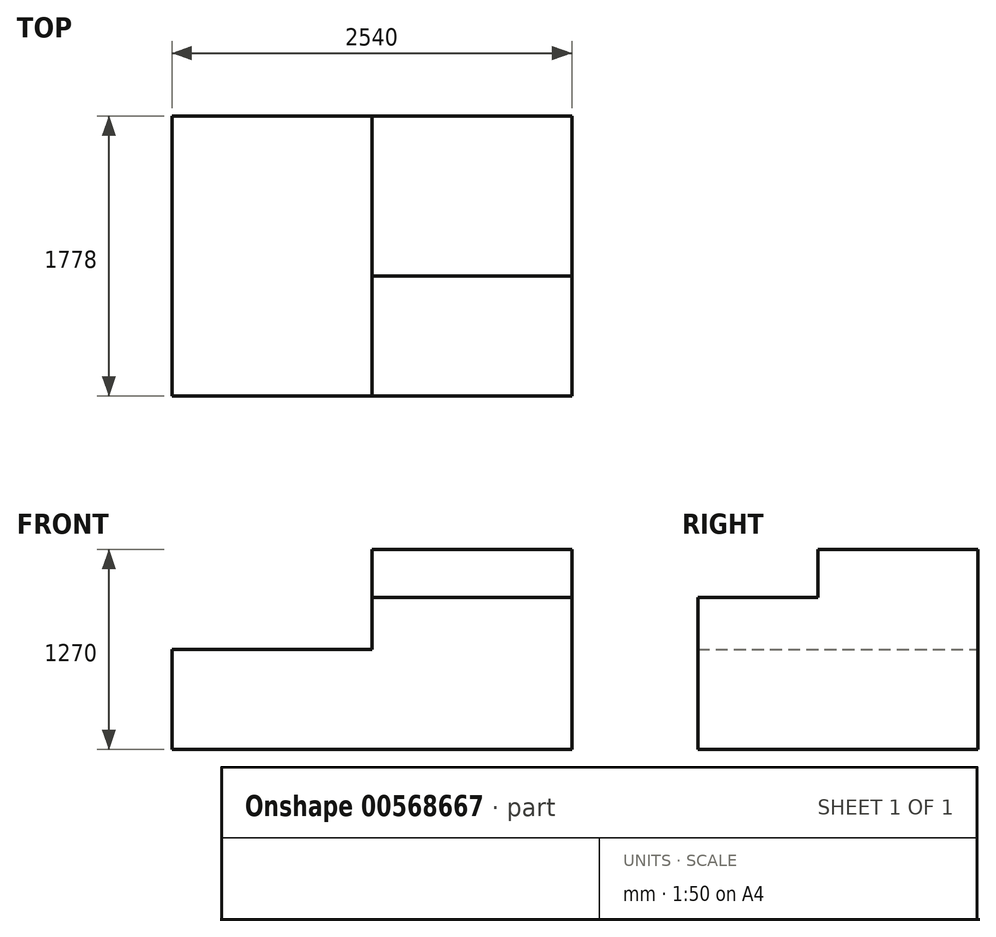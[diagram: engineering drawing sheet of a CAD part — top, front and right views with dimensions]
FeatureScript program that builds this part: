
annotation { "Feature Type Name" : "Feature", "Feature Type Description" : "" }
export const myFeature = defineFeature(function(context is Context, id is Id, definition is map)
    precondition{}
    {
        {
            var Q0;
            Q0=qCreatedBy(makeId("Top.planeOp"),FACE);
            var sketch = newSketch(context, id + "F0", { "sketchPlane" : qUnion([Q0])});
            skLineSegment(sketch, "E0.bottom", {"start": v(0, 0) * mm, "end": v(2540, 0) * mm});
            skLineSegment(sketch, "E0.top", {"start": v(0, -1778) * mm, "end": v(2540, -1778) * mm});
            skLineSegment(sketch, "E0.left", {"start": v(0, 0) * mm, "end": v(0, -1778) * mm});
            skLineSegment(sketch, "E0.right", {"start": v(2540, 0) * mm, "end": v(2540, -1778) * mm});
            skSolve(sketch);
        }
        {
            var Q0;
            Q0=makeQuery(id+"F0.imprint","IMPRINT",FACE,{"disambiguationData":[TD([[makeQuery(id+"F0.imprint","IMPRINT",EDGE,{"derivedFrom":sQuery(id+"F0.wireOp",EDGE,"E0.bottom")}),-1.0]])]});
            extrude(context, id + "F1", {"entities" : qUnion([Q0]), "depth" : 1270 * mm, "offsetDistance" : 25.4 * mm});
        }
        {
            var Q0;
            Q0=makeQuery(id+"F1.opExtrude","SWEPT_FACE",FACE,{"disambiguationData":[OSD([sQuery(id+"F0.wireOp",EDGE,"E0.left")])]});
            var sketch = newSketch(context, id + "F2", { "sketchPlane" : qUnion([Q0])});
            skLineSegment(sketch, "E1.bottom", {"start": v(1778, 0) * mm, "end": v(0, 0) * mm});
            skLineSegment(sketch, "E1.top", {"start": v(1778, 635) * mm, "end": v(0, 635) * mm});
            skLineSegment(sketch, "E1.left", {"start": v(1778, 0) * mm, "end": v(1778, 635) * mm});
            skLineSegment(sketch, "E1.right", {"start": v(0, 0) * mm, "end": v(0, 635) * mm});
            skSolve(sketch);
        }
        {
            var Q0;
            {var subQ0=sQuery(id+"F2.wireOp",EDGE,"E1.top");Q0=makeQuery(id+"F2.imprint","IMPRINT",FACE,{"disambiguationData":[TD([[makeQuery(id+"F2.imprint","IMPRINT",EDGE,{"derivedFrom":subQ0}),-1.0]])]});}
            extrude(context, id + "F3", {"entities" : qUnion([Q0]), "operationType" : NewBodyOperationType.REMOVE, "oppositeDirection" : true, "depth" : 1270 * mm, "offsetDistance" : 25.4 * mm});
        }
        {
            var Q0;
            Q0=makeQuery(id+"F1.opExtrude","CAP_FACE",FACE,{"disambiguationData":[OSD([sQuery(id+"F0.wireOp",EDGE,"E0.bottom"),sQuery(id+"F0.wireOp",EDGE,"E0.top"),sQuery(id+"F0.wireOp",EDGE,"E0.left"),sQuery(id+"F0.wireOp",EDGE,"E0.right")])],"isStart":false});
            var sketch = newSketch(context, id + "F4", { "sketchPlane" : qUnion([Q0])});
            skLineSegment(sketch, "E2.bottom", {"start": v(2540, 0) * mm, "end": v(1270, 0) * mm});
            skLineSegment(sketch, "E2.top", {"start": v(2540, -1016) * mm, "end": v(1270, -1016) * mm});
            skLineSegment(sketch, "E2.left", {"start": v(2540, 0) * mm, "end": v(2540, -1016) * mm});
            skLineSegment(sketch, "E2.right", {"start": v(1270, 0) * mm, "end": v(1270, -1016) * mm});
            skSolve(sketch);
        }
        {
            var Q0;
            {var subQ0=sQuery(id+"F4.wireOp",EDGE,"E2.top");Q0=makeQuery(id+"F4.imprint","IMPRINT",FACE,{"disambiguationData":[TD([[makeQuery(id+"F4.imprint","IMPRINT",EDGE,{"derivedFrom":subQ0}),1.0]])]});}
            extrude(context, id + "F5", {"entities" : qUnion([Q0]), "operationType" : NewBodyOperationType.REMOVE, "oppositeDirection" : true, "depth" : 304.8 * mm, "offsetDistance" : 25.4 * mm});
        }
    });
